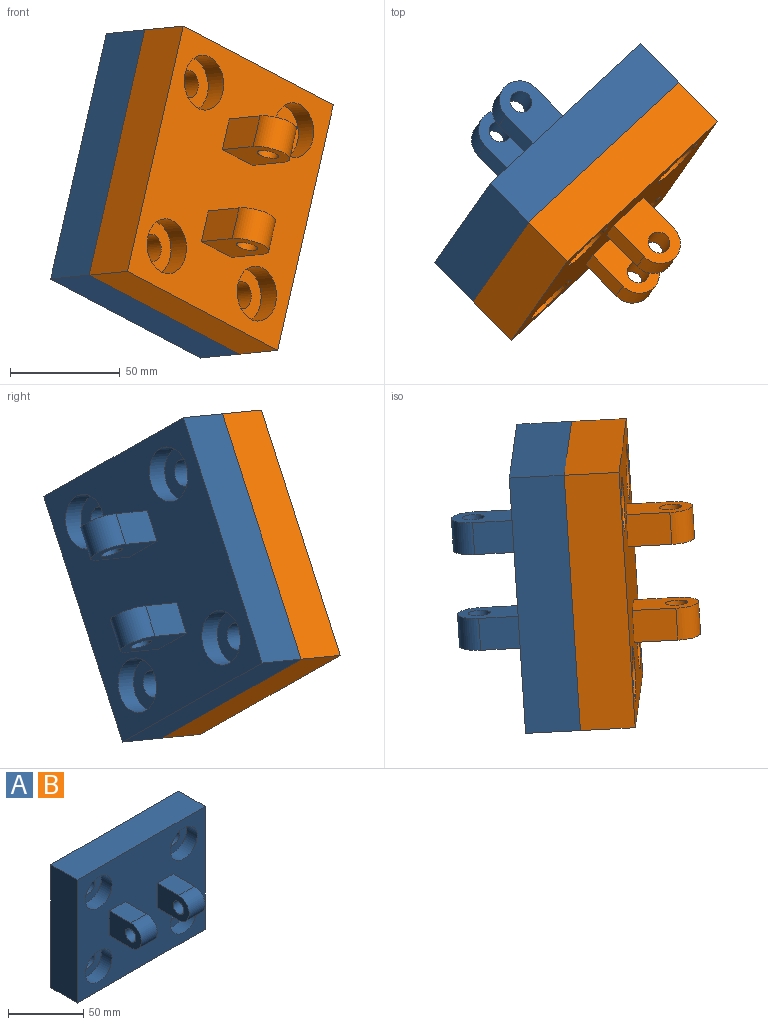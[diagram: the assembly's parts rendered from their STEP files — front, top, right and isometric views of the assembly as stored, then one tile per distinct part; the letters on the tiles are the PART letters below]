
ASSEMBLY  parts=2 mates=1
PART A: 30 faces, bbox 120x55x100 mm
  f0: plane 30x20mm, normal (-1,0,0), area 478.5mm2, adj f4,f5,f23,f28,f29
  f1: plane 30x20mm, normal (1,0,0), area 478.5mm2, adj f4,f5,f23,f28,f29
  f2: plane 30x20mm, normal (1,0,0), area 478.5mm2, adj f3,f5,f24,f26,f27
  f3: plane 20x15mm, normal (0,0,1), area 300mm2, adj f2,f5,f25,f27
  f4: plane 20x15mm, normal (0,0,-1), area 300mm2, adj f0,f1,f5,f29
  f5: plane 120x100mm, normal (0,-1,0), area 9436.5mm2, adj f0,f1,f2,f3,f4,f6,f7,f8
  f6: plane 100x25mm, normal (-1,0,0), area 2500mm2, adj f5,f7,f13,f14
  f7: plane 120x25mm, normal (0,0,-1), area 3000mm2, adj f5,f6,f8,f14
  f8: plane 100x25mm, normal (1,0,0), area 2500mm2, adj f5,f7,f13,f14
  f9: cylinder r=12.5mm len=25mm, axis (0,1,0), area 785.4mm2, adj f5,f16
  f10: cylinder r=12.5mm len=25mm, axis (0,1,0), area 785.4mm2, adj f5,f22
  f11: cylinder r=12.5mm len=25mm, axis (0,1,0), area 785.4mm2, adj f5,f20
  f12: cylinder r=12.5mm len=25mm, axis (0,1,0), area 785.4mm2, adj f5,f18
  f13: plane 120x25mm, normal (0,0,1), area 3000mm2, adj f5,f6,f8,f14
  f14: plane 120x100mm, normal (0,1,0), area 11509.1mm2, adj f6,f7,f8,f13,f15,f17,f19,f21
  f15: cylinder r=6.25mm len=15mm, axis (0,1,0), area 589mm2, adj f14,f16
  f16: plane 25x25mm, normal (0,-1,0), area 368.2mm2, adj f9,f15
  f17: cylinder r=6.25mm len=15mm, axis (0,1,0), area 589mm2, adj f14,f18
  f18: plane 25x25mm, normal (0,-1,0), area 368.2mm2, adj f12,f17
  f19: cylinder r=6.25mm len=15mm, axis (0,1,0), area 589mm2, adj f14,f20
  f20: plane 25x25mm, normal (0,-1,0), area 368.2mm2, adj f11,f19
  f21: cylinder r=6.25mm len=15mm, axis (0,1,0), area 589mm2, adj f14,f22
  f22: plane 25x25mm, normal (0,-1,0), area 368.2mm2, adj f10,f21
  f23: plane 20x15mm, normal (0,0,1), area 300mm2, adj f0,f1,f5,f29
  f24: plane 20x15mm, normal (0,0,-1), area 300mm2, adj f2,f5,f25,f27
  f25: plane 30x20mm, normal (-1,0,0), area 478.5mm2, adj f3,f5,f24,f26,f27
  f26: cylinder r=5mm len=15mm, axis (-1,0,0), area 471.2mm2, adj f2,f25
  f27: cylinder r=10mm len=20mm, axis (-1,0,0), area 471.2mm2, adj f2,f3,f24,f25
  f28: cylinder r=5mm len=15mm, axis (-1,0,0), area 471.2mm2, adj f0,f1
  f29: cylinder r=10mm len=20mm, axis (-1,0,0), area 471.2mm2, adj f0,f1,f4,f23
PART B: same geometry as A
PLACE A rot(axis=(-0.77,-0.34,-0.54),158.4deg) t=(-127.65,-18.08,-93.33)mm
PLACE B rot(axis=(0.29,-0.82,0.5),81.9deg) t=(-94.68,12.58,-110.67)mm
MATE revolute B.f11 <-> A.f9  axis (-0.7,0.71,-0.07) through (-142.81,-37.54,-140.21)mm
